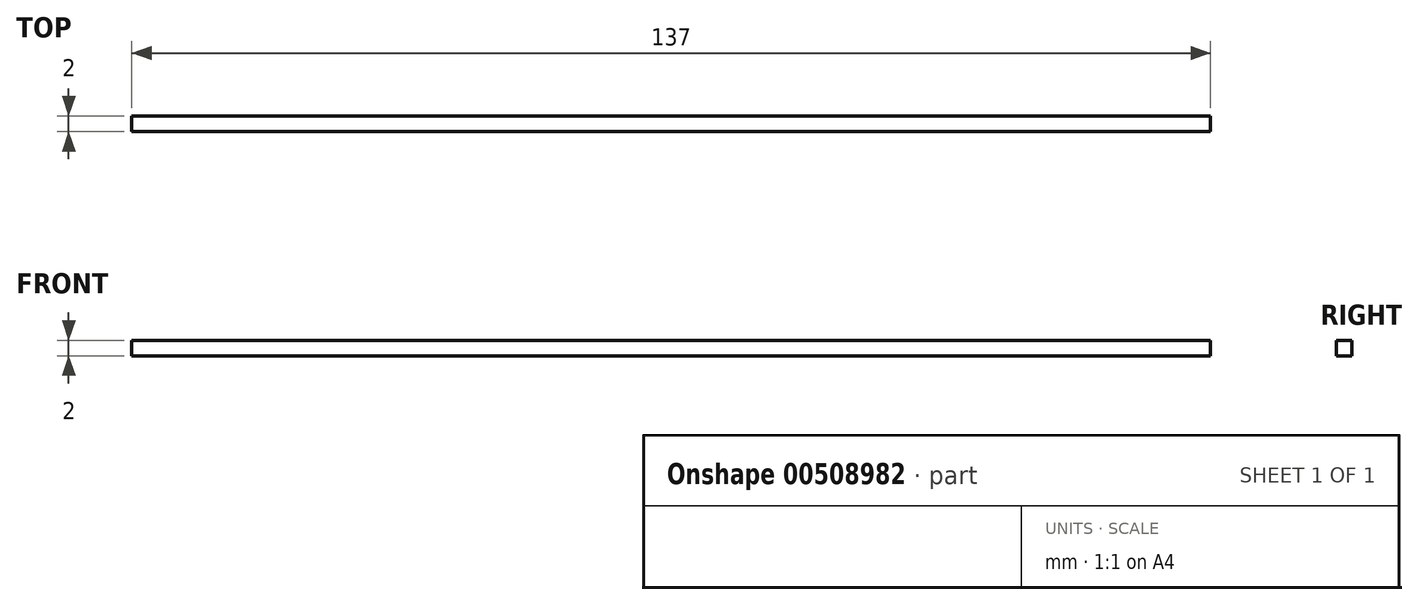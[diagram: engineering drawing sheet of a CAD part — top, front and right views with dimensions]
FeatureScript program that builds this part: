
annotation { "Feature Type Name" : "Feature", "Feature Type Description" : "" }
export const myFeature = defineFeature(function(context is Context, id is Id, definition is map)
    precondition{}
    {
        {
            var Q0;
            Q0=qCreatedBy(makeId("Top.planeOp"),FACE);
            var sketch = newSketch(context, id + "F0", { "sketchPlane" : qUnion([Q0])});
            skLineSegment(sketch, "E0.bottom", {"start": v(-68.5, 1) * mm, "end": v(68.5, 1) * mm});
            skLineSegment(sketch, "E0.top", {"start": v(-68.5, -1) * mm, "end": v(68.5, -1) * mm});
            skLineSegment(sketch, "E0.left", {"start": v(-68.5, 1) * mm, "end": v(-68.5, -1) * mm});
            skLineSegment(sketch, "E0.right", {"start": v(68.5, 1) * mm, "end": v(68.5, -1) * mm});
            skPoint(sketch, "E0.middle", {"position": v(0, 0) * mm});
            skSolve(sketch);
        }
        {
            var Q0;
            Q0 = qSketchRegion(id + "F0", true);
            extrude(context, id + "F1", {"entities" : qUnion([Q0]), "depth" : 2 * mm});
        }
    });
